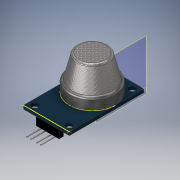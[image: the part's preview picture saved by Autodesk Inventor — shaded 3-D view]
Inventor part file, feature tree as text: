
AUTODESK INVENTOR PART (.ipt)
format: ipt  version: 2017.2 (Build 212223000, 223)  size: 243,200 bytes
history: native  units: in
note: dims shown in document units (in); Inventor stores cm internally (conversion verified against a paired STEP export)
features: sketch x11, extrude x5, fillet x2, plane x1, revolve x1, hole x1
ambient origin geometry x8: Origin, YZ Plane, XZ Plane, XY Plane, X Axis, Y Axis, Z Axis, Center Point
bodies: Solid1 (feature_tree)
feature tree (21):
  extrude  "Extrusion1"  Depth=0.7874in
  sketch  "Sketch2"  dims[d2=0.0591in d3=0.0in d7=0.7874in d8=0.1969in d9=0.0in]
  extrude  "Extrusion2"  Depth=0.7874in
  sketch  "Sketch4"  dims[d22=0.2559in d23=90.0deg]
  fillet  "Fillet1"  Radius=0.1969in
  sketch  "Sketch5"  dims[d24=0.0394in d26=0.0197in]
  plane  "Work Plane6"
  revolve  "Revolution1"  [1 undecoded]
  fillet  "Fillet2"  Radius=0.3937in
  extrude  "Extrusion3"  TaperAngle=90.0deg  [1 undecoded]
  sketch  "Sketch10"  dims[d62=0.1575in d63=0.0in]
  sketch  "Sketch11"  dims[d64=0.0197in]
  hole  "Hole1"  [1 undecoded]
  extrude  "Extrusion4"  Depth=0.1969in TaperAngle=0.0deg
  extrude  "Extrusion5"  Depth=0.1181in
  sketch  "Sketch1"  dims[d0=1.2795in d1=0.7874in]
  sketch  "Sketch3"  dims[d13=0.0394in d20=0.315in d21=0.3937in]
  sketch  "Sketch8"  dims[d28=1.9685in d30=360.0deg d32=0.1969in d33=0.0in]
  sketch  "Sketch9"  dims[d41=0.1181in d42=0.75in d43=0.375in d44=0.25in d45=0.5635in d46=1.0in d47=0.8108in d51=0.1181in]
  sketch  "Sketch12"  dims[d65=0.0197in]
  sketch  "Sketch13"  dims[d66=0.0197in d67=0.0197in d68=0.2362in d69=0.0394in d70=0.0in d71=0.0in d35=1.0in d36=1.0in]
note: 3 required parameter values undecoded (feature->parameter linkage not recoverable at this tier; creation-order binding heuristic only, values carry confidence <= 0.55)